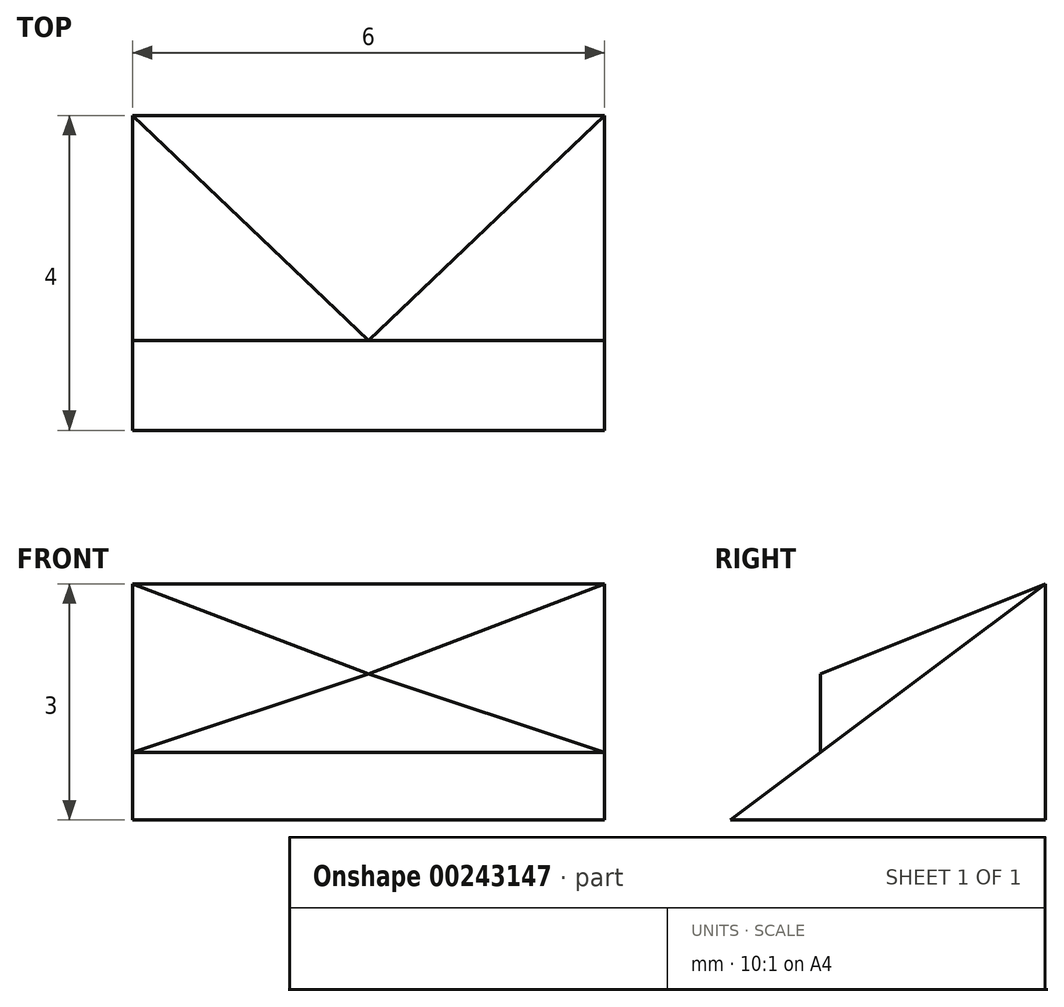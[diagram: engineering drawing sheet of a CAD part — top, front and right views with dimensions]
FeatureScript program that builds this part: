
annotation { "Feature Type Name" : "Feature", "Feature Type Description" : "" }
export const myFeature = defineFeature(function(context is Context, id is Id, definition is map)
    precondition{}
    {
        {
            var Q0;
            Q0=qCreatedBy(makeId("Right.planeOp"),FACE);
            var sketch = newSketch(context, id + "F0", { "sketchPlane" : qUnion([Q0])});
            skLineSegment(sketch, "E0", {"start": v(0, 0) * mm, "end": v(4, 0) * mm});
            skLineSegment(sketch, "E1", {"start": v(4, 0) * mm, "end": v(4, 3) * mm});
            skLineSegment(sketch, "E2", {"start": v(4, 3) * mm, "end": v(0, 0) * mm});
            skSolve(sketch);
        }
        {
            var Q0;
            Q0=qSketchRegion(id+"F0",true);
            extrude(context, id + "F1", {"entities" : qUnion([Q0]), "depth" : 6 * mm});
        }
        {
            var Q0;
            Q0=makeQuery(id+"F1.opExtrude","CAP_FACE",FACE,{"disambiguationData":[OSD([sQuery(id+"F0.wireOp",EDGE,"E0"),sQuery(id+"F0.wireOp",EDGE,"E1"),sQuery(id+"F0.wireOp",EDGE,"E2")])],"isStart":false});
            var sketch = newSketch(context, id + "F2", { "sketchPlane" : qUnion([Q0])});
            skLineSegment(sketch, "E3", {"start": v(0, 0) * mm, "end": v(1.14, 0) * mm});
            skLineSegment(sketch, "E4", {"start": v(1.14, 0) * mm, "end": v(1.14, 0.86) * mm});
            skSolve(sketch);
        }
        {
            var Q0;
            Q0=makeQuery(id+"F1.opExtrude","SWEPT_FACE",FACE,{"disambiguationData":[OSD([sQuery(id+"F0.wireOp",EDGE,"E2")])]});
            var sketch = newSketch(context, id + "F3", { "sketchPlane" : qUnion([Q0])});
            skPoint(sketch, "E5.0", {"position": v(6, 1.43) * mm});
            skLineSegment(sketch, "E6", {"start": v(6, 1.43) * mm, "end": v(0, 1.43) * mm});
            skSolve(sketch);
        }
        {
            var Q0;
            Q0=sQuery(id+"F2.wireOp",VERTEX,"E4.start");
            var Q1;
            Q1=sQuery(id+"F3.wireOp",VERTEX,"E5.0");
            var Q2;
            Q2=sQuery(id+"F3.wireOp",VERTEX,"E6.end");
            cPlane(context, id + "F4", {"entities" : qUnion([Q0, Q1, Q2]), "cplaneType" : CPlaneType.THREE_POINT, "offset" : 25 * mm, "width" : 150 * mm, "height" : 150 * mm});
        }
        {
            var Q0;
            Q0=qCreatedBy(id+"F4.planeOp",FACE);
            var sketch = newSketch(context, id + "F5", { "sketchPlane" : qUnion([Q0])});
            skPoint(sketch, "E7.0", {"position": v(0, 0.86) * mm});
            skPoint(sketch, "E8.0", {"position": v(-6, 0.86) * mm});
            skLineSegment(sketch, "E9", {"start": v(0, 0.86) * mm, "end": v(-6, 0.86) * mm});
            skLineSegment(sketch, "E10", {"start": v(-3, 0.86) * mm, "end": v(-3, 1.86) * mm, "construction": true});
            skLineSegment(sketch, "E11", {"start": v(-3, 1.86) * mm, "end": v(0, 0.86) * mm});
            skLineSegment(sketch, "E12", {"start": v(-3, 1.86) * mm, "end": v(-6, 0.86) * mm});
            skSolve(sketch);
        }
        {
            var Q0;
            Q0=makeQuery(id+"F1.opExtrude","CAP_VERTEX",VERTEX,{"disambiguationData":[OSD([sQuery(id+"F0.wireOp",EDGE,"E1"),sQuery(id+"F0.wireOp",EDGE,"E2")])],"isStart":true});
            var Q1;
            Q1=sQuery(id+"F5.wireOp",VERTEX,"E12.start");
            var Q2;
            Q2=sQuery(id+"F5.wireOp",VERTEX,"E7.0");
            cPlane(context, id + "F6", {"entities" : qUnion([Q0, Q1, Q2]), "cplaneType" : CPlaneType.THREE_POINT, "offset" : 25 * mm, "width" : 150 * mm, "height" : 150 * mm});
        }
        {
            var Q0;
            Q0=qCreatedBy(id+"F6.planeOp",FACE);
            var sketch = newSketch(context, id + "F7", { "sketchPlane" : qUnion([Q0])});
            skPoint(sketch, "E13.0", {"position": v(0, 5) * mm});
            skPoint(sketch, "E13.1", {"position": v(3.1, 2.03) * mm});
            skPoint(sketch, "E13.2", {"position": v(0, 1.43) * mm});
            skLineSegment(sketch, "E14", {"start": v(0, 5) * mm, "end": v(3.1, 2.03) * mm});
            skLineSegment(sketch, "E15", {"start": v(3.1, 2.03) * mm, "end": v(0, 1.43) * mm});
            skLineSegment(sketch, "E16", {"start": v(0, 1.43) * mm, "end": v(0, 5) * mm});
            skSolve(sketch);
        }
        {
            var Q0;
            Q0=sQuery(id+"F7.wireOp",VERTEX,"E13.1");
            var Q1;
            Q1=sQuery(id+"F5.wireOp",VERTEX,"E8.0");
            var Q2;
            Q2=makeQuery(id+"F1.opExtrude","CAP_VERTEX",VERTEX,{"disambiguationData":[OSD([sQuery(id+"F0.wireOp",EDGE,"E1"),sQuery(id+"F0.wireOp",EDGE,"E2")])],"isStart":false});
            cPlane(context, id + "F8", {"entities" : qUnion([Q0, Q1, Q2]), "cplaneType" : CPlaneType.THREE_POINT, "offset" : 25 * mm, "width" : 150 * mm, "height" : 150 * mm});
        }
        {
            var Q0;
            Q0=qCreatedBy(id+"F8.planeOp",FACE);
            var sketch = newSketch(context, id + "F9", { "sketchPlane" : qUnion([Q0])});
            skPoint(sketch, "E17.0", {"position": v(5.8, -5) * mm});
            skPoint(sketch, "E17.1", {"position": v(2.7, -2.03) * mm});
            skPoint(sketch, "E17.2", {"position": v(5.8, -1.43) * mm});
            skLineSegment(sketch, "E18", {"start": v(2.7, -2.03) * mm, "end": v(5.8, -5) * mm});
            skLineSegment(sketch, "E19", {"start": v(5.8, -1.43) * mm, "end": v(2.7, -2.03) * mm});
            skLineSegment(sketch, "E20", {"start": v(5.8, -5) * mm, "end": v(5.8, -1.43) * mm});
            skSolve(sketch);
        }
        {
            var Q0;
            {var subQ0=sQuery(id+"F2.wireOp",EDGE,"E4");Q0=makeQuery(id+"F2.imprint","IMPRINT",FACE,{"disambiguationData":[TD([[makeQuery(id+"F2.imprint","IMPRINT",EDGE,{"derivedFrom":subQ0}),-1.0]])]});}
            var sketch = newSketch(context, id + "F10", { "sketchPlane" : qUnion([Q0])});
            skPoint(sketch, "E21.0", {"position": v(4, 3) * mm});
            skPoint(sketch, "E22.0", {"position": v(1.14, 0.86) * mm});
            skPoint(sketch, "E23.0", {"position": v(1.14, 1.86) * mm});
            skLineSegment(sketch, "E24", {"start": v(1.14, 0.86) * mm, "end": v(1.14, 1.86) * mm});
            skLineSegment(sketch, "E25", {"start": v(4, 3) * mm, "end": v(1.14, 1.86) * mm});
            skLineSegment(sketch, "E26", {"start": v(1.14, 0.86) * mm, "end": v(4, 3) * mm});
            skSolve(sketch);
        }
        {
            var Q0;
            Q0=qSketchRegion(id+"F10",true);
            extrude(context, id + "F11", {"entities" : qUnion([Q0]), "operationType" : NewBodyOperationType.ADD, "oppositeDirection" : true, "depth" : 6 * mm});
        }
        {
            var Q0;
            Q0=qSketchRegion(id+"F9",true);
            extrude(context, id + "F12", {"entities" : qUnion([Q0]), "operationType" : NewBodyOperationType.REMOVE, "oppositeDirection" : true, "depth" : 25 * mm});
        }
        {
            var Q0;
            Q0=qSketchRegion(id+"F7",true);
            extrude(context, id + "F13", {"entities" : qUnion([Q0]), "operationType" : NewBodyOperationType.REMOVE, "depth" : 25 * mm});
        }
    });
